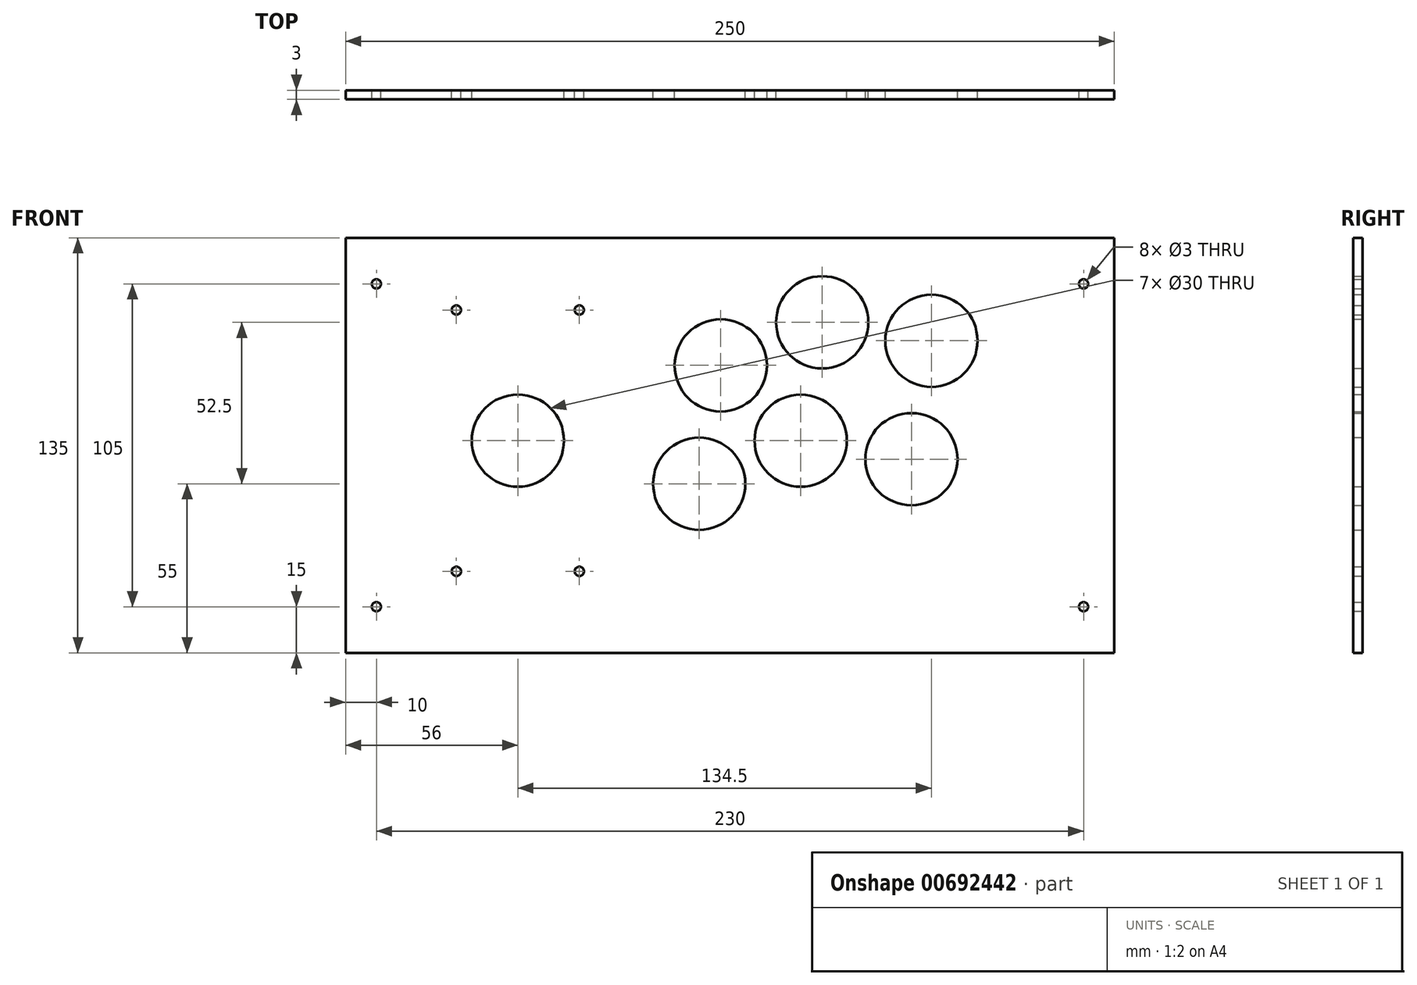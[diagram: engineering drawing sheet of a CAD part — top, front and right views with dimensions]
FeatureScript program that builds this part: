
annotation { "Feature Type Name" : "Feature", "Feature Type Description" : "" }
export const myFeature = defineFeature(function(context is Context, id is Id, definition is map)
    precondition{}
    {
        {
            var Q0;
            Q0=qCreatedBy(makeId("Front.planeOp"),FACE);
            var sketch = newSketch(context, id + "F0", { "sketchPlane" : qUnion([Q0])});
            skLineSegment(sketch, "E0.bottom", {"start": v(125, 67.5) * mm, "end": v(-125, 67.5) * mm});
            skLineSegment(sketch, "E0.top", {"start": v(125, -67.5) * mm, "end": v(-125, -67.5) * mm});
            skLineSegment(sketch, "E0.left", {"start": v(125, 67.5) * mm, "end": v(125, -67.5) * mm});
            skLineSegment(sketch, "E0.right", {"start": v(-125, 67.5) * mm, "end": v(-125, -67.5) * mm});
            skPoint(sketch, "E0.middle", {"position": v(0, 0) * mm});
            skCircle(sketch, "E1", {"center": v(-69, 1.5) * mm, "radius": 15 * mm});
            skCircle(sketch, "E2", {"center": v(-10, -12.5) * mm, "radius": 15 * mm});
            skCircle(sketch, "E3", {"center": v(-3, 26) * mm, "radius": 15 * mm});
            skCircle(sketch, "E4", {"center": v(30, 40) * mm, "radius": 15 * mm});
            skCircle(sketch, "E5", {"center": v(23, 1.5) * mm, "radius": 15 * mm});
            skCircle(sketch, "E6", {"center": v(65.5, 34) * mm, "radius": 15 * mm});
            skCircle(sketch, "E7", {"center": v(59, -4.5) * mm, "radius": 15 * mm});
            skCircle(sketch, "E8", {"center": v(-89, -41) * mm, "radius": 1.5 * mm});
            skCircle(sketch, "E9", {"center": v(-89, 44) * mm, "radius": 1.5 * mm});
            skCircle(sketch, "E10", {"center": v(-49, 44) * mm, "radius": 1.5 * mm});
            skCircle(sketch, "E11", {"center": v(-49, -41) * mm, "radius": 1.5 * mm});
            skCircle(sketch, "E12", {"center": v(-115, 52.5) * mm, "radius": 1.5 * mm});
            skCircle(sketch, "E13", {"center": v(-115, -52.5) * mm, "radius": 1.5 * mm});
            skCircle(sketch, "E14", {"center": v(115, -52.5) * mm, "radius": 1.5 * mm});
            skCircle(sketch, "E15", {"center": v(115, 52.5) * mm, "radius": 1.5 * mm});
            skSolve(sketch);
        }
        {
            var Q0;
            Q0=makeQuery(id+"F0.imprint","IMPRINT",FACE,{"disambiguationData":[TD([[makeQuery(id+"F0.imprint","IMPRINT",EDGE,{"derivedFrom":sQuery(id+"F0.wireOp",EDGE,"E0.bottom")}),1.0]])]});
            extrude(context, id + "F1", {"entities" : qUnion([Q0]), "depth" : 3 * mm, "offsetDistance" : 25 * mm});
        }
    });
